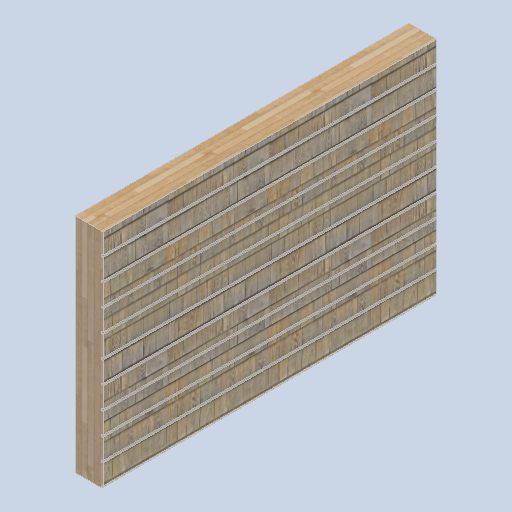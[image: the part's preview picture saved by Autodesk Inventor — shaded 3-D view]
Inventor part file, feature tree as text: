
AUTODESK INVENTOR PART (.ipt)
format: ipt  version: 2024.2 (Build 282272000, 272)  size: 541,184 bytes
history: native  units: mm
features: extrude x2, sketch x2
ambient origin geometry x8: Origin, YZ Plane, XZ Plane, XY Plane, X Axis, Y Axis, Z Axis, Center Point
bodies: Solid1 (feature_tree)
feature tree (4):
  extrude  "Extrusion1"  Depth=3000.0mm
  extrude  "Extrusion2"  Depth=250.0mm TaperAngle=0.0deg
  sketch  "Sketch1"  dims[d0=2000.0mm d1=3000.0mm]
  sketch  "Sketch3"  dims[d2=90.0deg d3=250.0mm d4=0.0mm d14=180.0mm d15=180.0mm d16=180.0mm d17=180.0mm d18=180.0mm d19=180.0mm d20=180.0mm d21=180.0mm d22=180.0mm d23=180.0mm d24=0.0mm d25=0.0mm]
